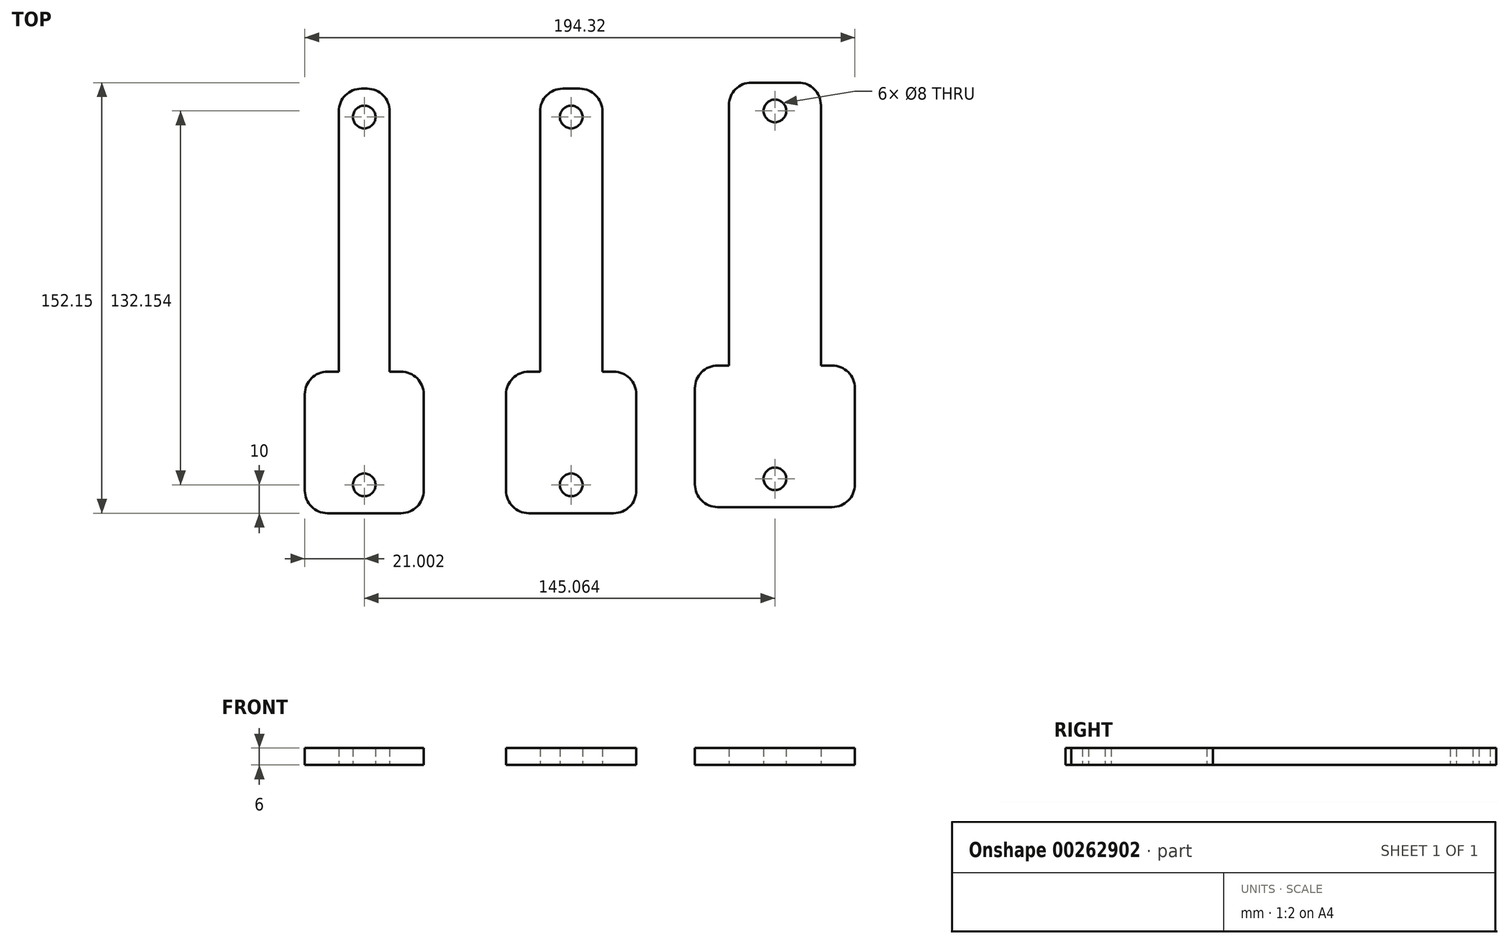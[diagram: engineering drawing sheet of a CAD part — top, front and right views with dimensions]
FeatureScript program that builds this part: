
annotation { "Feature Type Name" : "Feature", "Feature Type Description" : "" }
export const myFeature = defineFeature(function(context is Context, id is Id, definition is map)
    precondition{}
    {
        {
            var Q0;
            Q0=qCreatedBy(makeId("Top.planeOp"),FACE);
            var sketch = newSketch(context, id + "F0", { "sketchPlane" : qUnion([Q0])});
            skLineSegment(sketch, "E0.bottom", {"start": v(-38.53, 150) * mm, "end": v(-36.53, 150) * mm});
            skLineSegment(sketch, "E0.left", {"start": v(-46.53, 142) * mm, "end": v(-46.53, 50) * mm});
            skLineSegment(sketch, "E0.right", {"start": v(-28.53, 142) * mm, "end": v(-28.53, 50) * mm});
            skLineSegment(sketch, "E1.bottom", {"start": v(-50.53, 50) * mm, "end": v(-46.53, 50) * mm});
            skLineSegment(sketch, "E1.top", {"start": v(-50.53, 0) * mm, "end": v(-24.53, 0) * mm});
            skLineSegment(sketch, "E1.left", {"start": v(-58.53, 42) * mm, "end": v(-58.53, 8) * mm});
            skLineSegment(sketch, "E1.right", {"start": v(-16.53, 42) * mm, "end": v(-16.53, 8) * mm});
            skCircle(sketch, "E2", {"center": v(-37.53, 140) * mm, "radius": 4 * mm});
            skPoint(sketch, "E2.centerSnap0", {"position": v(-37.53, 150) * mm});
            skCircle(sketch, "E3", {"center": v(-37.53, 10) * mm, "radius": 4 * mm});
            skPoint(sketch, "E3.centerSnap0", {"position": v(-37.53, 0) * mm});
            skLineSegment(sketch, "E4.trimOffspring", {"start": v(-28.53, 50) * mm, "end": v(-24.53, 50) * mm});
            skLineSegment(sketch, "E5", {"start": v(-37.53, 150) * mm, "end": v(-37.53, 0) * mm, "construction": true});
            skPoint(sketch, "E6.visualSharp", {"position": v(-46.53, 150) * mm});
            skArc(sketch, "E6.filletArc", {"start": v(-38.53, 150) * mm, "mid": v(-44.19, 147.66) * mm, "end": v(-46.53, 142) * mm});
            skPoint(sketch, "E7.visualSharp", {"position": v(-28.53, 150) * mm});
            skArc(sketch, "E7.filletArc", {"start": v(-28.53, 142) * mm, "mid": v(-30.87, 147.66) * mm, "end": v(-36.53, 150) * mm});
            skPoint(sketch, "E8.visualSharp", {"position": v(-16.53, 0) * mm});
            skArc(sketch, "E8.filletArc", {"start": v(-24.53, 0) * mm, "mid": v(-18.87, 2.34) * mm, "end": v(-16.53, 8) * mm});
            skPoint(sketch, "E9.visualSharp", {"position": v(-58.53, 0) * mm});
            skArc(sketch, "E9.filletArc", {"start": v(-58.53, 8) * mm, "mid": v(-56.19, 2.34) * mm, "end": v(-50.53, 0) * mm});
            skPoint(sketch, "E10.visualSharp", {"position": v(-58.53, 50) * mm});
            skArc(sketch, "E10.filletArc", {"start": v(-50.53, 50) * mm, "mid": v(-56.19, 47.66) * mm, "end": v(-58.53, 42) * mm});
            skPoint(sketch, "E11.visualSharp", {"position": v(-16.53, 50) * mm});
            skArc(sketch, "E11.filletArc", {"start": v(-16.53, 42) * mm, "mid": v(-18.87, 47.66) * mm, "end": v(-24.53, 50) * mm});
            skSolve(sketch);
        }
        {
            var Q0;
            Q0 = qSketchRegion(id + "F0", true);
            extrude(context, id + "F1", {"entities" : qUnion([Q0]), "depth" : 6 * mm});
        }
        {
            var Q0;
            Q0=qCreatedBy(makeId("Top.planeOp"),FACE);
            var sketch = newSketch(context, id + "F2", { "sketchPlane" : qUnion([Q0])});
            skLineSegment(sketch, "E12.bottom", {"start": v(32.57, 150) * mm, "end": v(38.57, 150) * mm});
            skLineSegment(sketch, "E12.left", {"start": v(24.57, 142) * mm, "end": v(24.57, 50) * mm});
            skLineSegment(sketch, "E12.right", {"start": v(46.57, 142) * mm, "end": v(46.57, 50) * mm});
            skLineSegment(sketch, "E13.bottom", {"start": v(20.57, 50) * mm, "end": v(24.57, 50) * mm});
            skLineSegment(sketch, "E13.top", {"start": v(20.57, 0) * mm, "end": v(50.57, 0) * mm});
            skLineSegment(sketch, "E13.left", {"start": v(12.57, 42) * mm, "end": v(12.57, 8) * mm});
            skLineSegment(sketch, "E13.right", {"start": v(58.57, 42) * mm, "end": v(58.57, 8) * mm});
            skCircle(sketch, "E14", {"center": v(35.57, 140) * mm, "radius": 4 * mm});
            skPoint(sketch, "E14.centerSnap0", {"position": v(35.57, 150) * mm});
            skCircle(sketch, "E15", {"center": v(35.57, 10) * mm, "radius": 4 * mm});
            skPoint(sketch, "E15.centerSnap0", {"position": v(35.57, 0) * mm});
            skLineSegment(sketch, "E16.trimOffspring", {"start": v(46.57, 50) * mm, "end": v(50.57, 50) * mm});
            skLineSegment(sketch, "E17", {"start": v(35.57, 150) * mm, "end": v(35.57, 0) * mm, "construction": true});
            skPoint(sketch, "E18.visualSharp", {"position": v(24.57, 150) * mm});
            skArc(sketch, "E18.filletArc", {"start": v(32.57, 150) * mm, "mid": v(26.92, 147.66) * mm, "end": v(24.57, 142) * mm});
            skPoint(sketch, "E19.visualSharp", {"position": v(46.57, 150) * mm});
            skArc(sketch, "E19.filletArc", {"start": v(46.57, 142) * mm, "mid": v(44.23, 147.66) * mm, "end": v(38.57, 150) * mm});
            skPoint(sketch, "E20.visualSharp", {"position": v(58.57, 0) * mm});
            skArc(sketch, "E20.filletArc", {"start": v(50.57, 0) * mm, "mid": v(56.23, 2.34) * mm, "end": v(58.57, 8) * mm});
            skPoint(sketch, "E21.visualSharp", {"position": v(12.57, 0) * mm});
            skArc(sketch, "E21.filletArc", {"start": v(12.57, 8) * mm, "mid": v(14.92, 2.34) * mm, "end": v(20.57, 0) * mm});
            skPoint(sketch, "E22.visualSharp", {"position": v(12.57, 50) * mm});
            skArc(sketch, "E22.filletArc", {"start": v(20.57, 50) * mm, "mid": v(14.92, 47.66) * mm, "end": v(12.57, 42) * mm});
            skPoint(sketch, "E23.visualSharp", {"position": v(58.57, 50) * mm});
            skArc(sketch, "E23.filletArc", {"start": v(58.57, 42) * mm, "mid": v(56.23, 47.66) * mm, "end": v(50.57, 50) * mm});
            skSolve(sketch);
        }
        {
            var Q0;
            Q0 = qSketchRegion(id + "F2", true);
            extrude(context, id + "F3", {"entities" : qUnion([Q0]), "depth" : 6 * mm});
        }
        {
            var Q0;
            Q0=qCreatedBy(makeId("Top.planeOp"),FACE);
            var sketch = newSketch(context, id + "F4", { "sketchPlane" : qUnion([Q0])});
            skLineSegment(sketch, "E24.bottom", {"start": v(99.29, 152.15) * mm, "end": v(115.79, 152.15) * mm});
            skLineSegment(sketch, "E24.left", {"start": v(91.29, 144.15) * mm, "end": v(91.29, 52.15) * mm});
            skLineSegment(sketch, "E24.right", {"start": v(123.79, 144.15) * mm, "end": v(123.79, 52.15) * mm});
            skLineSegment(sketch, "E25.bottom", {"start": v(87.29, 52.15) * mm, "end": v(91.29, 52.15) * mm});
            skLineSegment(sketch, "E25.top", {"start": v(87.29, 2.15) * mm, "end": v(127.79, 2.15) * mm});
            skLineSegment(sketch, "E25.left", {"start": v(79.29, 44.15) * mm, "end": v(79.29, 10.15) * mm});
            skLineSegment(sketch, "E25.right", {"start": v(135.79, 44.15) * mm, "end": v(135.79, 10.15) * mm});
            skCircle(sketch, "E26", {"center": v(107.54, 142.15) * mm, "radius": 4 * mm});
            skPoint(sketch, "E26.centerSnap0", {"position": v(107.54, 152.15) * mm});
            skCircle(sketch, "E27", {"center": v(107.54, 12.15) * mm, "radius": 4 * mm});
            skPoint(sketch, "E27.centerSnap0", {"position": v(107.54, 2.15) * mm});
            skLineSegment(sketch, "E28.trimOffspring", {"start": v(123.79, 52.15) * mm, "end": v(127.79, 52.15) * mm});
            skLineSegment(sketch, "E29", {"start": v(107.54, 152.15) * mm, "end": v(107.54, 2.15) * mm, "construction": true});
            skPoint(sketch, "E30.visualSharp", {"position": v(91.29, 152.15) * mm});
            skArc(sketch, "E30.filletArc", {"start": v(99.29, 152.15) * mm, "mid": v(93.63, 149.81) * mm, "end": v(91.29, 144.15) * mm});
            skPoint(sketch, "E31.visualSharp", {"position": v(123.79, 152.15) * mm});
            skArc(sketch, "E31.filletArc", {"start": v(123.79, 144.15) * mm, "mid": v(121.44, 149.81) * mm, "end": v(115.79, 152.15) * mm});
            skPoint(sketch, "E32.visualSharp", {"position": v(135.79, 2.15) * mm});
            skArc(sketch, "E32.filletArc", {"start": v(127.79, 2.15) * mm, "mid": v(133.44, 4.5) * mm, "end": v(135.79, 10.15) * mm});
            skPoint(sketch, "E33.visualSharp", {"position": v(79.29, 2.15) * mm});
            skArc(sketch, "E33.filletArc", {"start": v(79.29, 10.15) * mm, "mid": v(81.63, 4.5) * mm, "end": v(87.29, 2.15) * mm});
            skPoint(sketch, "E34.visualSharp", {"position": v(79.29, 52.15) * mm});
            skArc(sketch, "E34.filletArc", {"start": v(87.29, 52.15) * mm, "mid": v(81.63, 49.81) * mm, "end": v(79.29, 44.15) * mm});
            skPoint(sketch, "E35.visualSharp", {"position": v(135.79, 52.15) * mm});
            skArc(sketch, "E35.filletArc", {"start": v(135.79, 44.15) * mm, "mid": v(133.44, 49.81) * mm, "end": v(127.79, 52.15) * mm});
            skSolve(sketch);
        }
        {
            var Q0;
            Q0 = qSketchRegion(id + "F4", true);
            extrude(context, id + "F5", {"entities" : qUnion([Q0]), "depth" : 6 * mm});
        }
    });
